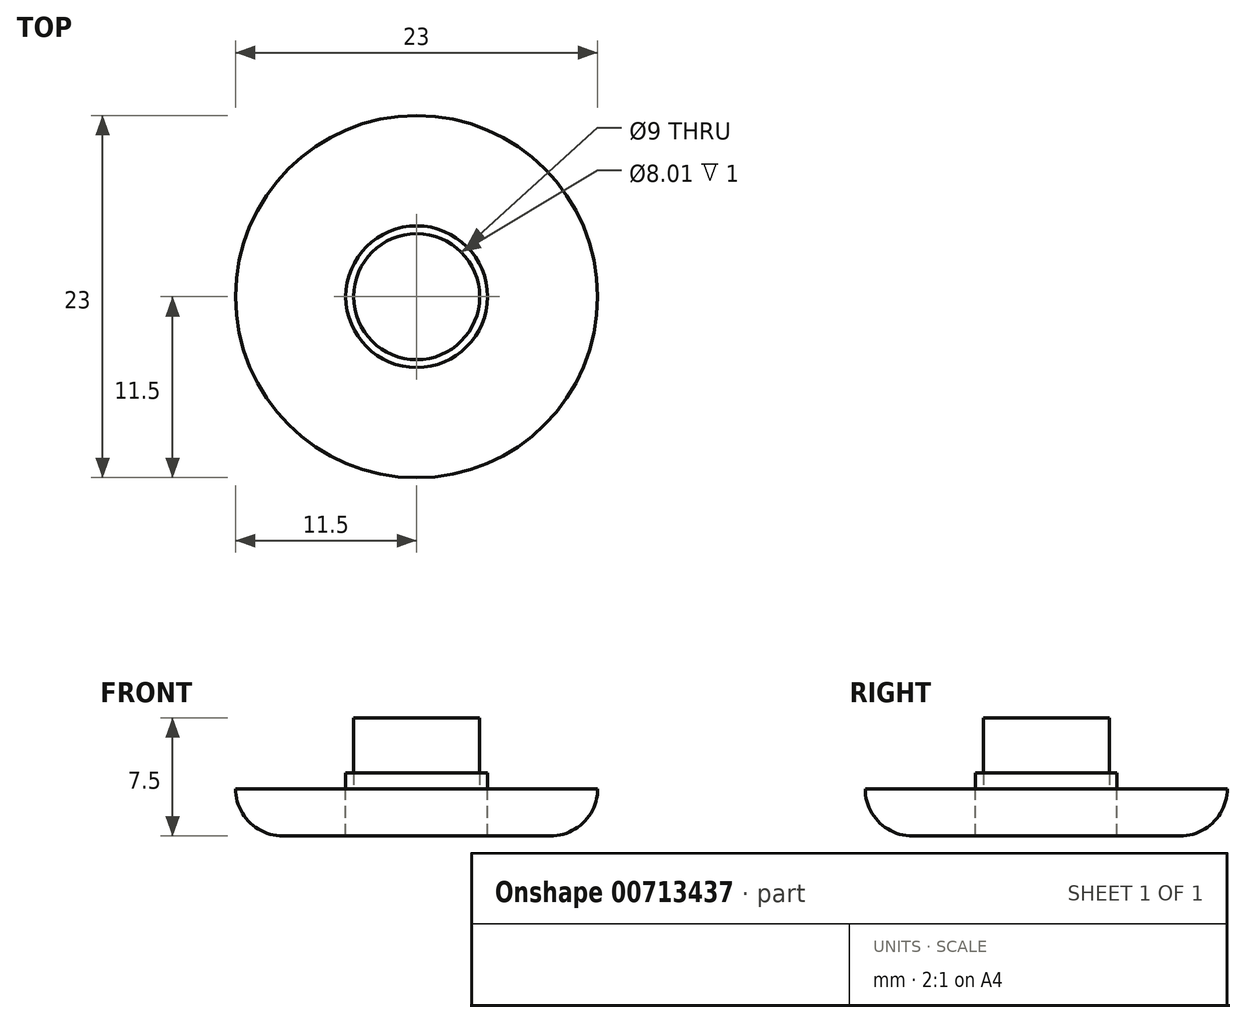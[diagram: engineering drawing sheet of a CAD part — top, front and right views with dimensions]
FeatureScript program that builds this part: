
annotation { "Feature Type Name" : "Feature", "Feature Type Description" : "" }
export const myFeature = defineFeature(function(context is Context, id is Id, definition is map)
    precondition{}
    {
        {
            var Q0;
            Q0=qCreatedBy(makeId("Top.planeOp"),FACE);
            var sketch = newSketch(context, id + "F0", { "sketchPlane" : qUnion([Q0])});
            skCircle(sketch, "E0", {"center": v(0, 0) * mm, "radius": 11.5 * mm});
            skCircle(sketch, "E1", {"center": v(0, 0) * mm, "radius": 4.5 * mm});
            skCircle(sketch, "E2", {"center": v(0, 0) * mm, "radius": 4 * mm});
            skSolve(sketch);
        }
        {
            var Q0;
            Q0=makeQuery(id+"F0.imprint","IMPRINT",FACE,{"disambiguationData":[TD([[makeQuery(id+"F0.imprint","IMPRINT",EDGE,{"derivedFrom":sQuery(id+"F0.wireOp",EDGE,"E1")}),1.0]])]});
            extrude(context, id + "F1", {"entities" : qUnion([Q0]), "depth" : 1 * mm, "offsetDistance" : 25 * mm});
        }
        {
            var Q0;
            Q0=makeQuery(id+"F0.imprint","IMPRINT",FACE,{"disambiguationData":[TD([[makeQuery(id+"F0.imprint","IMPRINT",EDGE,{"derivedFrom":sQuery(id+"F0.wireOp",EDGE,"E2")}),1.0]])]});
            extrude(context, id + "F2", {"entities" : qUnion([Q0]), "depth" : 4.5 * mm, "offsetDistance" : 25 * mm});
        }
        {
            var Q0;
            Q0=makeQuery(id+"F0.imprint","IMPRINT",FACE,{"disambiguationData":[TD([[makeQuery(id+"F0.imprint","IMPRINT",EDGE,{"derivedFrom":sQuery(id+"F0.wireOp",EDGE,"E0")}),1.0]])]});
            extrude(context, id + "F3", {"entities" : qUnion([Q0]), "operationType" : NewBodyOperationType.ADD, "oppositeDirection" : true, "depth" : 3 * mm, "offsetDistance" : 25 * mm});
        }
        {
            var Q0;
            Q0=makeQuery(id+"F0.imprint","IMPRINT",FACE,{"disambiguationData":[TD([[makeQuery(id+"F0.imprint","IMPRINT",EDGE,{"derivedFrom":sQuery(id+"F0.wireOp",EDGE,"E2")}),1.0]])]});
            var Q1;
            Q1=makeQuery(id+"F0.imprint","IMPRINT",FACE,{"disambiguationData":[TD([[makeQuery(id+"F0.imprint","IMPRINT",EDGE,{"derivedFrom":sQuery(id+"F0.wireOp",EDGE,"E1")}),1.0]])]});
            extrude(context, id + "F4", {"entities" : qUnion([Q0, Q1]), "oppositeDirection" : true, "depth" : 3 * mm, "offsetDistance" : 25 * mm});
        }
        {
            var Q0;
            Q0=makeQuery(id+"F3.opExtrude","CAP_EDGE",EDGE,{"disambiguationData":[OSD([sQuery(id+"F0.wireOp",EDGE,"E0")])],"isStart":false});
            fillet(context, id + "F5", {"entities" : qUnion([Q0]), "radius" : 3 * mm, "tangentPropagation" : true, "allowEdgeOverflow" : false});
        }
    });
